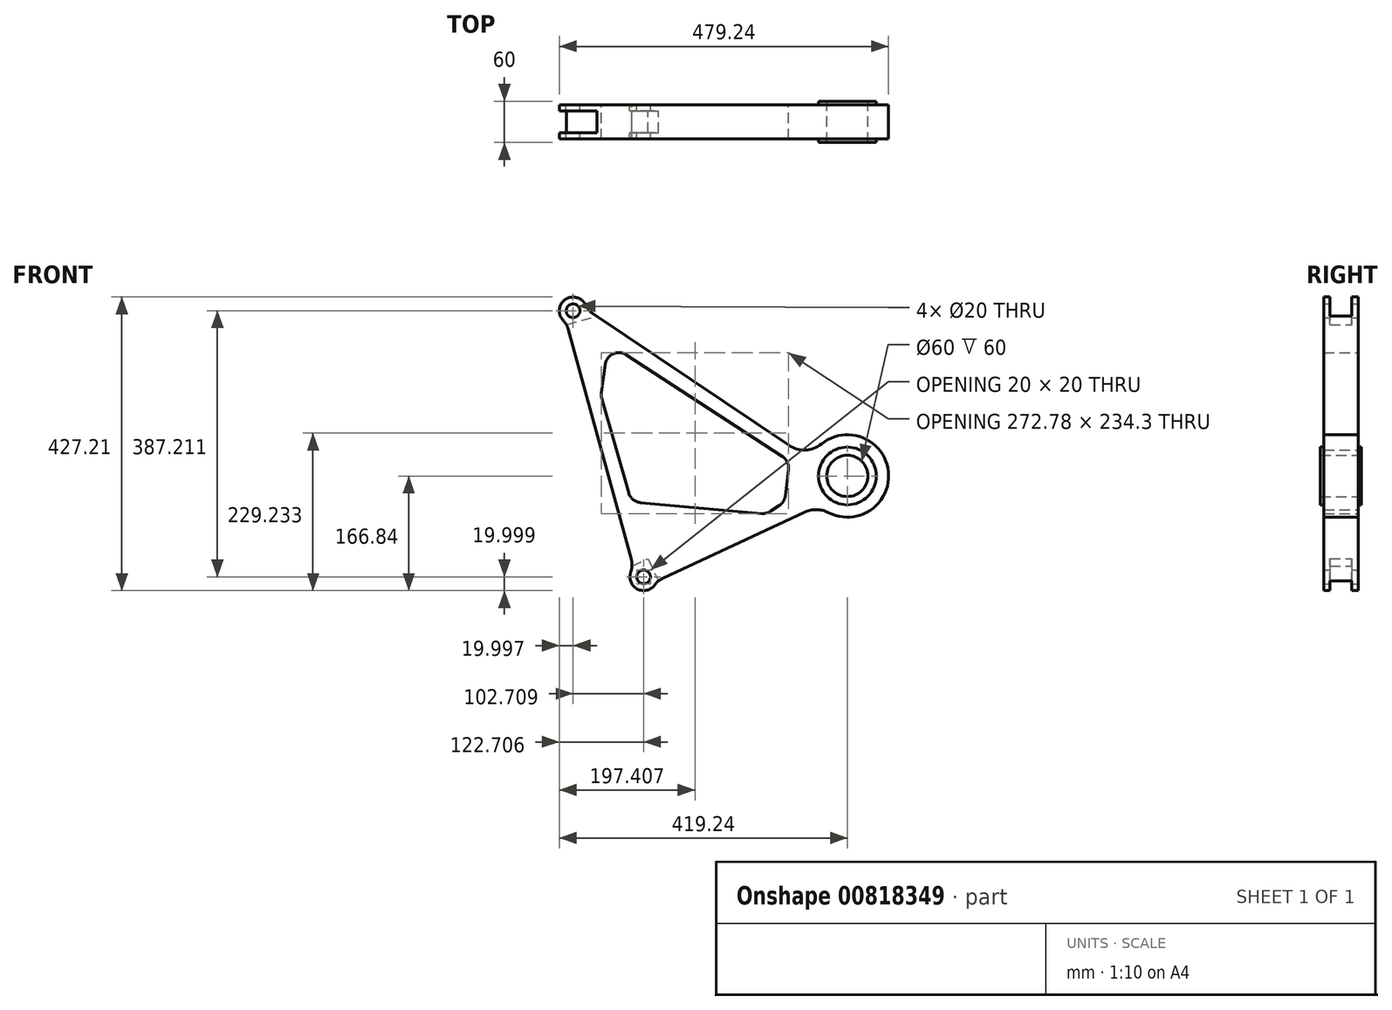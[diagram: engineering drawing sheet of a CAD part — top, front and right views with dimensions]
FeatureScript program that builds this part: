
annotation { "Feature Type Name" : "Feature", "Feature Type Description" : "" }
export const myFeature = defineFeature(function(context is Context, id is Id, definition is map)
    precondition{}
    {
        {
            var Q0;
            Q0=qCreatedBy(makeId("Front.planeOp"),FACE);
            var sketch = newSketch(context, id + "F0", { "sketchPlane" : qUnion([Q0])});
            skArc(sketch, "E0", {"start": v(-27.4, -53.38) * mm, "mid": v(59.68, 6.17) * mm, "end": v(-37.74, 46.64) * mm});
            skLineSegment(sketch, "E1", {"start": v(-370.8, 236.85) * mm, "end": v(-85.25, 44.56) * mm});
            skLineSegment(sketch, "E2", {"start": v(-406.3, 213.6) * mm, "end": v(-314.5, -121.58) * mm});
            skLineSegment(sketch, "E3", {"start": v(-268.68, -148.91) * mm, "end": v(-62.58, -52.72) * mm});
            skPoint(sketch, "E4.visualSharp", {"position": v(-54.93, 24.14) * mm});
            skArc(sketch, "E4.filletArc", {"start": v(-85.25, 44.56) * mm, "mid": v(-61.15, 37.77) * mm, "end": v(-37.74, 46.64) * mm});
            skPoint(sketch, "E5.visualSharp", {"position": v(-41.81, -43.03) * mm});
            skArc(sketch, "E5.filletArc", {"start": v(-27.4, -53.38) * mm, "mid": v(-44.91, -48.97) * mm, "end": v(-62.58, -52.72) * mm});
            skArc(sketch, "E6", {"start": v(-381.16, 248.92) * mm, "mid": v(-410.6, 256.83) * mm, "end": v(-413.64, 226.49) * mm});
            skPoint(sketch, "E7.visualSharp", {"position": v(-408.83, 222.82) * mm});
            skArc(sketch, "E7.filletArc", {"start": v(-406.3, 213.6) * mm, "mid": v(-409.16, 220.5) * mm, "end": v(-413.64, 226.49) * mm});
            skPoint(sketch, "E8.visualSharp", {"position": v(-379.37, 242.63) * mm});
            skArc(sketch, "E8.filletArc", {"start": v(-381.16, 248.92) * mm, "mid": v(-376.8, 242.19) * mm, "end": v(-370.8, 236.85) * mm});
            skArc(sketch, "E9", {"start": v(-315.3, -139.9) * mm, "mid": v(-305.94, -164.5) * mm, "end": v(-280.32, -158.54) * mm});
            skPoint(sketch, "E10.visualSharp", {"position": v(-311.28, -133.33) * mm});
            skArc(sketch, "E10.filletArc", {"start": v(-315.3, -139.9) * mm, "mid": v(-313.46, -130.8) * mm, "end": v(-314.5, -121.58) * mm});
            skPoint(sketch, "E11.visualSharp", {"position": v(-277.52, -153.04) * mm});
            skArc(sketch, "E11.filletArc", {"start": v(-268.68, -148.91) * mm, "mid": v(-275.11, -152.98) * mm, "end": v(-280.32, -158.54) * mm});
            skCircle(sketch, "E12", {"center": v(-296.53, -146.84) * mm, "radius": 10 * mm});
            skCircle(sketch, "E13", {"center": v(-399.24, 240.37) * mm, "radius": 10 * mm});
            skCircle(sketch, "E14", {"center": v(0, 0) * mm, "radius": 30 * mm});
            skSolve(sketch);
        }
        {
            var Q0;
            Q0=makeQuery(id+"F0.imprint","IMPRINT",FACE,{"disambiguationData":[TD([[makeQuery(id+"F0.imprint","IMPRINT",EDGE,{"derivedFrom":sQuery(id+"F0.wireOp",EDGE,"E0")}),1.0]])]});
            extrude(context, id + "F1", {"entities" : qUnion([Q0]), "depth" : 50 * mm, "offsetDistance" : 25 * mm});
        }
        {
            var Q0;
            Q0=qCreatedBy(makeId("Front.planeOp"),FACE);
            cPlane(context, id + "F2", {"entities" : qUnion([Q0]), "cplaneType" : CPlaneType.OFFSET, "offset" : 25 * mm, "width" : 150 * mm, "height" : 150 * mm});
        }
        {
            var Q0;
            Q0=makeQuery(id+"F1.opExtrude","SWEPT_FACE",FACE,{"disambiguationData":[OSD([sQuery(id+"F0.wireOp",EDGE,"E2")])]});
            var sketch = newSketch(context, id + "F3", { "sketchPlane" : qUnion([Q0])});
            skLineSegment(sketch, "E15", {"start": v(9, 320.53) * mm, "end": v(9, 367.5) * mm});
            skLineSegment(sketch, "E16", {"start": v(41, 367.5) * mm, "end": v(41, 320.53) * mm});
            skLineSegment(sketch, "E17.0", {"start": v(50, 313.34) * mm, "end": v(50, 327.72) * mm});
            skLineSegment(sketch, "E18", {"start": v(9, 320.53) * mm, "end": v(50, 320.53) * mm});
            skPoint(sketch, "E19.orphan", {"position": v(0, 320.53) * mm});
            skPoint(sketch, "E20.orphan", {"position": v(0, 327.72) * mm});
            skPoint(sketch, "E21.0.start.orphan", {"position": v(0, 313.34) * mm});
            skPoint(sketch, "E22.orphan", {"position": v(9, 313.34) * mm});
            skPoint(sketch, "E23.orphan", {"position": v(41, 313.34) * mm});
            skLineSegment(sketch, "E24", {"start": v(9, 367.5) * mm, "end": v(41, 367.5) * mm});
            skSolve(sketch);
        }
        {
            var Q0;
            Q0=makeQuery(id+"F3.imprint","IMPRINT",FACE,{"disambiguationData":[TD([[makeQuery(id+"F3.imprint","IMPRINT",EDGE,{"derivedFrom":sQuery(id+"F3.wireOp",EDGE,"E15")}),-1.0]])]});
            var Q1;
            Q1=makeQuery(id+"F3.imprint","IMPRINT",FACE,{"disambiguationData":[TD([[makeQuery(id+"F3.imprint","IMPRINT",EDGE,{"derivedFrom":sQuery(id+"F3.wireOp",EDGE,"NHGZ6CMz-R015-fZps-pOmO-vMtHGA6LpUAF")}),1.0]])]});
            extrude(context, id + "F4", {"entities" : qUnion([Q0, Q1]), "operationType" : NewBodyOperationType.REMOVE, "depth" : 36 * mm, "offsetDistance" : 25 * mm, "hasSecondDirection" : true, "secondDirectionOppositeDirection" : true, "secondDirectionDepth" : 36 * mm});
        }
        {
            var Q0;
            Q0=makeQuery(id+"F1.opExtrude","SWEPT_FACE",FACE,{"disambiguationData":[OSD([sQuery(id+"F0.wireOp",EDGE,"E3")])]});
            var sketch = newSketch(context, id + "F5", { "sketchPlane" : qUnion([Q0])});
            skSolve(sketch);
        }
        {
            var Q0;
            {var subQ0=sQuery(id+"F0.wireOp",EDGE,"E3");Q0=makeQuery(id+"F5.imprint","IMPRINT",FACE,{"disambiguationData":[TD([[makeQuery(id+"F5.imprint","IMPRINT",EDGE,{"derivedFrom":makeQuery(id+"F1.opExtrude","CAP_EDGE",EDGE,{"disambiguationData":[OSD([subQ0])],"isStart":true})}),1.0]])]});}
            cPlane(context, id + "F6", {"entities" : qUnion([Q0]), "cplaneType" : CPlaneType.OFFSET, "offset" : 0 * mm, "width" : 150 * mm, "height" : 150 * mm});
        }
        {
            var Q0;
            Q0=qCreatedBy(id+"F6.planeOp",FACE);
            var sketch = newSketch(context, id + "F7", { "sketchPlane" : qUnion([Q0])});
            skPoint(sketch, "E25.0", {"position": v(-314, 0) * mm});
            skPoint(sketch, "E26.0", {"position": v(-314, 50) * mm});
            skLineSegment(sketch, "E27", {"start": v(-378.34, 9) * mm, "end": v(-378.34, 41) * mm});
            skLineSegment(sketch, "E28", {"start": v(-378.34, 41) * mm, "end": v(-314, 41) * mm});
            skLineSegment(sketch, "E29", {"start": v(-314, 41) * mm, "end": v(-314, 9) * mm});
            skLineSegment(sketch, "E30", {"start": v(-378.34, 9) * mm, "end": v(-314, 9) * mm});
            skSolve(sketch);
        }
        {
            var Q0;
            Q0=makeQuery(id+"F7.imprint","IMPRINT",FACE,{"disambiguationData":[TD([[makeQuery(id+"F7.imprint","IMPRINT",EDGE,{"derivedFrom":sQuery(id+"F7.wireOp",EDGE,"E27")}),-1.0]])]});
            extrude(context, id + "F8", {"entities" : qUnion([Q0]), "operationType" : NewBodyOperationType.REMOVE, "oppositeDirection" : true, "depth" : 35 * mm, "offsetDistance" : 25 * mm, "hasSecondDirection" : true, "secondDirectionOppositeDirection" : false, "secondDirectionDepth" : 25 * mm});
        }
        {
            var Q0;
            Q0=makeQuery(id+"F1.opExtrude","CAP_FACE",FACE,{"disambiguationData":[OSD([sQuery(id+"F0.wireOp",EDGE,"E0"),sQuery(id+"F0.wireOp",EDGE,"E1"),sQuery(id+"F0.wireOp",EDGE,"E2"),sQuery(id+"F0.wireOp",EDGE,"E3"),sQuery(id+"F0.wireOp",EDGE,"E4.filletArc"),sQuery(id+"F0.wireOp",EDGE,"E5.filletArc"),sQuery(id+"F0.wireOp",EDGE,"E6"),sQuery(id+"F0.wireOp",EDGE,"E7.filletArc"),sQuery(id+"F0.wireOp",EDGE,"E8.filletArc"),sQuery(id+"F0.wireOp",EDGE,"E9"),sQuery(id+"F0.wireOp",EDGE,"E10.filletArc"),sQuery(id+"F0.wireOp",EDGE,"E11.filletArc"),sQuery(id+"F0.wireOp",EDGE,"E12"),sQuery(id+"F0.wireOp",EDGE,"E13"),sQuery(id+"F0.wireOp",EDGE,"E14")])],"isStart":false});
            var sketch = newSketch(context, id + "F9", { "sketchPlane" : qUnion([Q0])});
            skLineSegment(sketch, "E31", {"start": v(-358.61, 116.78) * mm, "end": v(-348.2, 193.61) * mm});
            skLineSegment(sketch, "E32", {"start": v(-348.2, 193.61) * mm, "end": v(-84.08, 21.53) * mm});
            skLineSegment(sketch, "E33", {"start": v(-84.08, 21.53) * mm, "end": v(-91.28, -37.7) * mm});
            skLineSegment(sketch, "E34", {"start": v(-91.28, -37.7) * mm, "end": v(-117.7, -55.3) * mm});
            skLineSegment(sketch, "E35", {"start": v(-117.7, -55.3) * mm, "end": v(-314.5, -37.7) * mm});
            skLineSegment(sketch, "E36", {"start": v(-314.5, -37.7) * mm, "end": v(-358.61, 116.78) * mm});
            skSolve(sketch);
        }
        {
            var Q0;
            Q0=makeQuery(id+"F9.imprint","IMPRINT",FACE,{"disambiguationData":[TD([[makeQuery(id+"F9.imprint","IMPRINT",EDGE,{"derivedFrom":sQuery(id+"F9.wireOp",EDGE,"FiySOdgB-WNFm-bZMc-sRs8-ynZFk20fW7co")}),1.0]])]});
            var Q1;
            Q1=makeQuery(id+"F9.imprint","IMPRINT",FACE,{"disambiguationData":[TD([[makeQuery(id+"F9.imprint","IMPRINT",EDGE,{"derivedFrom":sQuery(id+"F9.wireOp",EDGE,"E31")}),-1.0]])]});
            extrude(context, id + "F10", {"entities" : qUnion([Q0, Q1]), "operationType" : NewBodyOperationType.REMOVE, "oppositeDirection" : true, "depth" : 100 * mm, "offsetDistance" : 25 * mm});
        }
        {
            var Q0;
            Q0=makeQuery(id+"F10.boolean.opBoolean","COPY",EDGE,{"derivedFrom":makeQuery(id+"F10.opExtrude","SWEPT_EDGE",EDGE,{"disambiguationData":[OSD([sQuery(id+"F9.wireOp",EDGE,"E31"),sQuery(id+"F9.wireOp",EDGE,"E32")])]})});
            var Q1;
            Q1=makeQuery(id+"F10.boolean.opBoolean","COPY",EDGE,{"derivedFrom":makeQuery(id+"F10.opExtrude","SWEPT_EDGE",EDGE,{"disambiguationData":[OSD([sQuery(id+"F9.wireOp",EDGE,"E31"),sQuery(id+"F9.wireOp",EDGE,"E36")])]})});
            var Q2;
            Q2=makeQuery(id+"F10.boolean.opBoolean","COPY",EDGE,{"derivedFrom":makeQuery(id+"F10.opExtrude","SWEPT_EDGE",EDGE,{"disambiguationData":[OSD([sQuery(id+"F9.wireOp",EDGE,"E32"),sQuery(id+"F9.wireOp",EDGE,"E33")])]})});
            var Q3;
            Q3=makeQuery(id+"F10.boolean.opBoolean","COPY",EDGE,{"derivedFrom":makeQuery(id+"F10.opExtrude","SWEPT_EDGE",EDGE,{"disambiguationData":[OSD([sQuery(id+"F9.wireOp",EDGE,"E33"),sQuery(id+"F9.wireOp",EDGE,"E34")])]})});
            var Q4;
            Q4=makeQuery(id+"F10.boolean.opBoolean","COPY",EDGE,{"derivedFrom":makeQuery(id+"F10.opExtrude","SWEPT_EDGE",EDGE,{"disambiguationData":[OSD([sQuery(id+"F9.wireOp",EDGE,"E34"),sQuery(id+"F9.wireOp",EDGE,"E35")])]})});
            var Q5;
            Q5=makeQuery(id+"F10.boolean.opBoolean","COPY",EDGE,{"derivedFrom":makeQuery(id+"F10.opExtrude","SWEPT_EDGE",EDGE,{"disambiguationData":[OSD([sQuery(id+"F9.wireOp",EDGE,"E35"),sQuery(id+"F9.wireOp",EDGE,"E36")])]})});
            fillet(context, id + "F11", {"entities" : qUnion([Q0, Q1, Q2, Q3, Q4, Q5]), "radius" : 20 * mm, "tangentPropagation" : true, "allowEdgeOverflow" : false});
        }
        {
            var Q0;
            Q0=makeQuery(id+"F1.opExtrude","CAP_FACE",FACE,{"disambiguationData":[OSD([sQuery(id+"F0.wireOp",EDGE,"E0"),sQuery(id+"F0.wireOp",EDGE,"E1"),sQuery(id+"F0.wireOp",EDGE,"E2"),sQuery(id+"F0.wireOp",EDGE,"E3"),sQuery(id+"F0.wireOp",EDGE,"E4.filletArc"),sQuery(id+"F0.wireOp",EDGE,"E5.filletArc"),sQuery(id+"F0.wireOp",EDGE,"E6"),sQuery(id+"F0.wireOp",EDGE,"E7.filletArc"),sQuery(id+"F0.wireOp",EDGE,"E8.filletArc"),sQuery(id+"F0.wireOp",EDGE,"E9"),sQuery(id+"F0.wireOp",EDGE,"E10.filletArc"),sQuery(id+"F0.wireOp",EDGE,"E11.filletArc"),sQuery(id+"F0.wireOp",EDGE,"E12"),sQuery(id+"F0.wireOp",EDGE,"E13"),sQuery(id+"F0.wireOp",EDGE,"E14")])],"isStart":false});
            var sketch = newSketch(context, id + "F12", { "sketchPlane" : qUnion([Q0])});
            skCircle(sketch, "E37", {"center": v(0, 0) * mm, "radius": 42 * mm});
            skSolve(sketch);
        }
        {
            var Q0;
            Q0=makeQuery(id+"F12.imprint","IMPRINT",FACE,{"disambiguationData":[TD([[makeQuery(id+"F12.imprint","IMPRINT",EDGE,{"derivedFrom":sQuery(id+"F12.wireOp",EDGE,"E37")}),1.0]])]});
            extrude(context, id + "F13", {"entities" : qUnion([Q0]), "operationType" : NewBodyOperationType.ADD, "depth" : 5 * mm, "offsetDistance" : 25 * mm});
        }
        {
            var Q0;
            Q0=makeQuery(id+"F1.opExtrude","CAP_FACE",FACE,{"disambiguationData":[OSD([sQuery(id+"F0.wireOp",EDGE,"E0"),sQuery(id+"F0.wireOp",EDGE,"E1"),sQuery(id+"F0.wireOp",EDGE,"E2"),sQuery(id+"F0.wireOp",EDGE,"E3"),sQuery(id+"F0.wireOp",EDGE,"E4.filletArc"),sQuery(id+"F0.wireOp",EDGE,"E5.filletArc"),sQuery(id+"F0.wireOp",EDGE,"E6"),sQuery(id+"F0.wireOp",EDGE,"E7.filletArc"),sQuery(id+"F0.wireOp",EDGE,"E8.filletArc"),sQuery(id+"F0.wireOp",EDGE,"E9"),sQuery(id+"F0.wireOp",EDGE,"E10.filletArc"),sQuery(id+"F0.wireOp",EDGE,"E11.filletArc"),sQuery(id+"F0.wireOp",EDGE,"E12"),sQuery(id+"F0.wireOp",EDGE,"E13"),sQuery(id+"F0.wireOp",EDGE,"E14")])],"isStart":true});
            var sketch = newSketch(context, id + "F14", { "sketchPlane" : qUnion([Q0])});
            skCircle(sketch, "E38", {"center": v(0, 0) * mm, "radius": 42 * mm});
            skSolve(sketch);
        }
        {
            var Q0;
            Q0=makeQuery(id+"F14.imprint","IMPRINT",FACE,{"disambiguationData":[TD([[makeQuery(id+"F14.imprint","IMPRINT",EDGE,{"derivedFrom":sQuery(id+"F14.wireOp",EDGE,"E38")}),1.0]])]});
            extrude(context, id + "F15", {"entities" : qUnion([Q0]), "operationType" : NewBodyOperationType.ADD, "depth" : 5 * mm, "offsetDistance" : 25 * mm});
        }
        {
            var Q0;
            Q0=makeQuery(id+"F4.boolean.opBoolean","COPY",FACE,{"derivedFrom":makeQuery(id+"F4.opExtrude","CAP_FACE",FACE,{"disambiguationData":[OSD([sQuery(id+"F3.wireOp",EDGE,"E15"),sQuery(id+"F3.wireOp",EDGE,"E16"),sQuery(id+"F3.wireOp",EDGE,"E18"),sQuery(id+"F3.wireOp",EDGE,"E24")])],"isStart":true})});
            var sketch = newSketch(context, id + "F16", { "sketchPlane" : qUnion([Q0])});
            skLineSegment(sketch, "E39.0", {"start": v(9, 333.16) * mm, "end": v(41, 333.16) * mm});
            skLineSegment(sketch, "E40.0", {"start": v(41, 333.16) * mm, "end": v(41, 320.53) * mm});
            skLineSegment(sketch, "E41.0", {"start": v(9, 320.53) * mm, "end": v(41, 320.53) * mm});
            skLineSegment(sketch, "E42.0", {"start": v(9, 320.53) * mm, "end": v(9, 333.16) * mm});
            skSolve(sketch);
        }
        {
            var Q0;
            Q0 = qSketchRegion(id + "F16", true);
            extrude(context, id + "F17", {"entities" : qUnion([Q0]), "operationType" : NewBodyOperationType.REMOVE, "depth" : 25 * mm, "offsetDistance" : 25 * mm, "hasSecondDirection" : true, "secondDirectionOppositeDirection" : true, "secondDirectionDepth" : 25 * mm});
        }
    });
